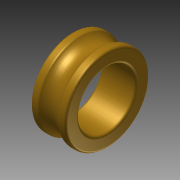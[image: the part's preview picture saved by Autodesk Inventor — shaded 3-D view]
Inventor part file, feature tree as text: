
AUTODESK INVENTOR PART (.ipt)
format: ipt  version: 2011 SP2 (Build 150309200, 309)  size: 169,472 bytes
history: native  units: mm
features: revolve x1, fillet x1, sketch x1
ambient origin geometry x8: Origin, YZ Plane, XZ Plane, XY Plane, X Axis, Y Axis, Z Axis, Center Point
bodies: Solid1 (feature_tree)
feature tree (3):
  revolve  "Revolution1"  [1 undecoded]
  fillet  "Fillet1"  Radius=25.0mm
  sketch  "Sketch1"  dims[d0=31.0mm d1=37.0mm d2=25.0mm d3=12.0mm d4=8.0mm d5=90.0deg d6=2.0mm]
note: 1 required parameter value undecoded (feature->parameter linkage not recoverable at this tier; creation-order binding heuristic only, values carry confidence <= 0.55)
